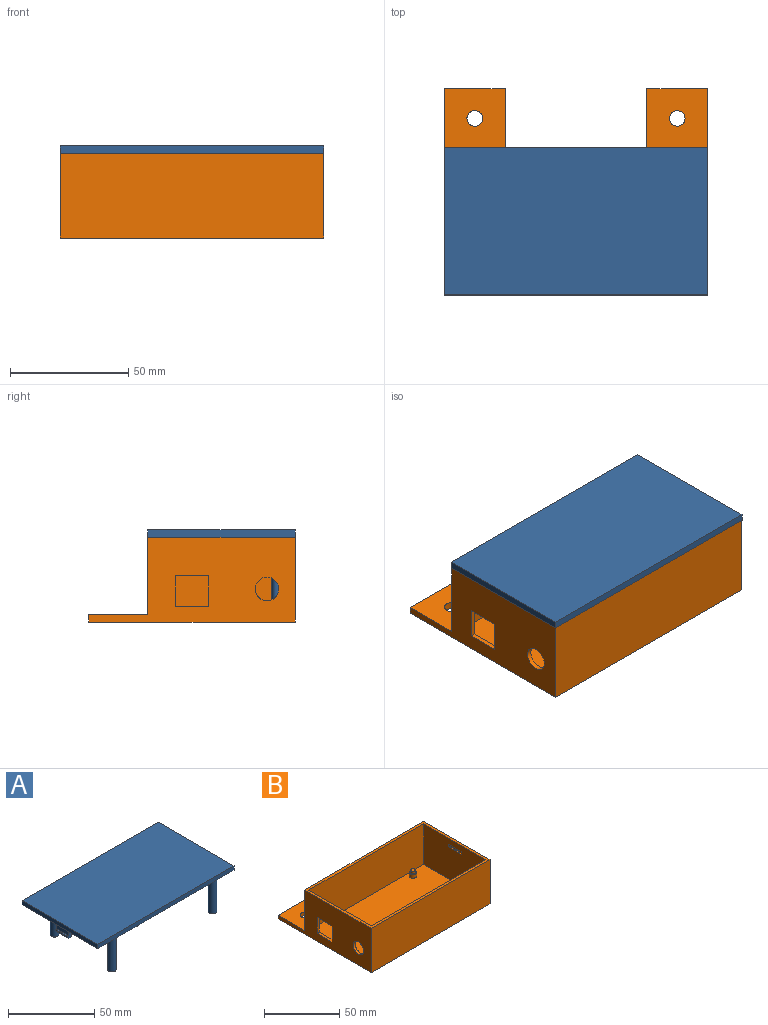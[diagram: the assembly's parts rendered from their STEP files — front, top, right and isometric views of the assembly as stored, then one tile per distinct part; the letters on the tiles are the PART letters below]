
ASSEMBLY  parts=2 mates=1
PART A: 50 faces, bbox 111.6x62.3x31 mm
  f0: plane 111.6x62.34mm, normal (0,0,-1), area 6748.6mm2, adj f1,f2,f3,f4,f10,f11,f12,f13
  f1: plane 111.6x3mm, normal (0,1,0), area 334.8mm2, adj f0,f2,f4,f5
  f2: plane 62.34x3mm, normal (-1,0,0), area 187mm2, adj f0,f1,f3,f5
  f3: plane 111.6x3mm, normal (0,-1,0), area 334.8mm2, adj f0,f2,f4,f5
  f4: plane 62.34x3mm, normal (1,0,0), area 187mm2, adj f0,f1,f3,f5
  f5: plane 111.6x62.34mm, normal (0,0,1), area 6957.1mm2, adj f1,f2,f3,f4
  f6: plane 10x2.5mm, normal (0,0,-1), area 25mm2, adj f7,f11,f12,f13
  f7: plane 10x1mm, normal (0.71,0,-0.71), area 14.1mm2, adj f6,f8,f12,f13
  f8: plane 10x1mm, normal (1,0,0), area 10mm2, adj f7,f9,f12,f13
  f9: plane 10x1mm, normal (0,0,1), area 10mm2, adj f8,f10,f12,f13
  f10: plane 10x5mm, normal (1,0,0), area 50mm2, adj f0,f9,f12,f13
  f11: plane 10x7mm, normal (-1,0,0), area 70mm2, adj f0,f6,f12,f13
  f12: plane 7x3.5mm, normal (0,-1,0), area 19mm2, adj f0,f6,f7,f8,f9,f10,f11
  f13: plane 7x3.5mm, normal (0,1,0), area 19mm2, adj f0,f6,f7,f8,f9,f10,f11
  f14: plane 10x5mm, normal (-1,0,0), area 50mm2, adj f0,f15,f20,f21
  f15: plane 10x1mm, normal (0,0,1), area 10mm2, adj f14,f16,f20,f21
  f16: plane 10x1mm, normal (-1,0,0), area 10mm2, adj f15,f17,f20,f21
  f17: plane 10x1mm, normal (-0.71,0,-0.71), area 14.1mm2, adj f16,f18,f20,f21
  f18: plane 10x2.5mm, normal (0,0,-1), area 25mm2, adj f17,f19,f20,f21
  f19: plane 10x7mm, normal (1,0,0), area 70mm2, adj f0,f18,f20,f21
  f20: plane 7x3.5mm, normal (0,-1,0), area 19mm2, adj f0,f14,f15,f16,f17,f18,f19
  f21: plane 7x3.5mm, normal (0,1,0), area 19mm2, adj f0,f14,f15,f16,f17,f18,f19
  f22: plane 2x2mm, normal (-1,0,0), area 4mm2, adj f0,f23,f25,f26
  f23: plane 10x2mm, normal (0,-1,0), area 20mm2, adj f0,f22,f24,f26
  f24: plane 2x2mm, normal (1,0,0), area 4mm2, adj f0,f23,f25,f26
  f25: plane 10x2mm, normal (0,1,0), area 20mm2, adj f0,f22,f24,f26
  f26: plane 10x2mm, normal (0,0,-1), area 20mm2, adj f22,f23,f24,f25
  f27: plane 2x2mm, normal (-1,0,0), area 4mm2, adj f0,f28,f30,f31
  f28: plane 10x2mm, normal (0,-1,0), area 20mm2, adj f0,f27,f29,f31
  f29: plane 2x2mm, normal (1,0,0), area 4mm2, adj f0,f28,f30,f31
  f30: plane 10x2mm, normal (0,1,0), area 20mm2, adj f0,f27,f29,f31
  f31: plane 10x2mm, normal (0,0,-1), area 20mm2, adj f27,f28,f29,f30
  f32: plane 2x2mm, normal (1,0,0), area 4mm2, adj f0,f33,f35,f36
  f33: plane 10x2mm, normal (0,1,0), area 20mm2, adj f0,f32,f34,f36
  f34: plane 2x2mm, normal (-1,0,0), area 4mm2, adj f0,f33,f35,f36
  f35: plane 10x2mm, normal (0,-1,0), area 20mm2, adj f0,f32,f34,f36
  f36: plane 10x2mm, normal (0,0,-1), area 20mm2, adj f32,f33,f34,f35
  f37: plane 2x2mm, normal (-1,0,0), area 4mm2, adj f0,f38,f40,f41
  f38: plane 10x2mm, normal (0,-1,0), area 20mm2, adj f0,f37,f39,f41
  f39: plane 2x2mm, normal (1,0,0), area 4mm2, adj f0,f38,f40,f41
  f40: plane 10x2mm, normal (0,1,0), area 20mm2, adj f0,f37,f39,f41
  f41: plane 10x2mm, normal (0,0,-1), area 20mm2, adj f37,f38,f39,f40
  f42: plane 5x5mm, normal (0,0,-1), area 19.6mm2, adj f43
  f43: cylinder r=2.5mm len=28mm, axis (0,0,1), area 439.8mm2, adj f0,f42
  f44: plane 5x5mm, normal (0,0,-1), area 19.6mm2, adj f45
  f45: cylinder r=2.5mm len=28mm, axis (0,0,1), area 439.8mm2, adj f0,f44
  f46: plane 5x5mm, normal (0,0,-1), area 19.6mm2, adj f47
  f47: cylinder r=2.5mm len=28mm, axis (0,0,1), area 439.8mm2, adj f0,f46
  f48: plane 5x5mm, normal (0,0,-1), area 19.6mm2, adj f49
  f49: cylinder r=2.5mm len=28mm, axis (0,0,1), area 439.8mm2, adj f0,f48
PART B: 50 faces, bbox 111.6x87.3x36 mm
  f0: plane 58.34x33mm, normal (1,0,0), area 1639.5mm2, adj f2,f11,f13,f14,f25,f26,f27,f28
  f1: plane 87.34x36mm, normal (-1,0,0), area 2058.7mm2, adj f14,f15,f17,f19,f23,f24,f25,f26
  f2: plane 107.6x58.34mm, normal (0,0,1), area 6198.8mm2, adj f0,f3,f5,f7,f9,f11,f12,f13
  f3: cylinder r=2.5mm len=5mm, axis (0,0,-1), area 47.1mm2, adj f2,f4
  f4: plane 5x5mm, normal (0,0,1), area 12.6mm2, adj f3,f40
  f5: cylinder r=2.5mm len=5mm, axis (0,0,-1), area 47.1mm2, adj f2,f6
  f6: plane 5x5mm, normal (0,0,1), area 12.6mm2, adj f5,f42
  f7: cylinder r=2.5mm len=5mm, axis (0,0,-1), area 47.1mm2, adj f2,f8
  f8: plane 5x5mm, normal (0,0,1), area 12.6mm2, adj f7,f44
  f9: cylinder r=2.5mm len=5mm, axis (0,0,-1), area 47.1mm2, adj f2,f10
  f10: plane 5x5mm, normal (0,0,1), area 12.6mm2, adj f9,f46
  f11: plane 107.6x33mm, normal (0,-1,0), area 3550.8mm2, adj f0,f2,f12,f14
  f12: plane 58.34x33mm, normal (-1,0,0), area 1900mm2, adj f2,f11,f13,f14,f30,f32,f33,f34
  f13: plane 107.6x33mm, normal (0,1,0), area 3550.8mm2, adj f0,f2,f12,f14
  f14: plane 111.6x62.34mm, normal (0,0,1), area 679.8mm2, adj f0,f1,f11,f12,f13,f19,f22,f23
  f15: plane 25.8x3mm, normal (0,1,0), area 77.4mm2, adj f1,f16,f17,f24
  f16: plane 25x3mm, normal (1,0,0), area 75mm2, adj f15,f17,f19,f24
  f17: plane 111.6x87.34mm, normal (0,0,-1), area 8178.7mm2, adj f1,f15,f16,f18,f19,f20,f22,f23
  f18: plane 25.8x3mm, normal (0,1,0), area 77.4mm2, adj f17,f20,f21,f22
  f19: plane 111.6x36mm, normal (0,1,0), area 3862.8mm2, adj f1,f14,f16,f17,f20,f21,f22,f24
  f20: plane 25x3mm, normal (-1,0,0), area 75mm2, adj f17,f18,f19,f21
  f21: plane 25.8x25mm, normal (0,0,1), area 610.8mm2, adj f18,f19,f20,f22,f49
  f22: plane 87.34x36mm, normal (1,0,0), area 2319.2mm2, adj f14,f17,f18,f19,f21,f23
  f23: plane 111.6x36mm, normal (0,-1,0), area 4017.6mm2, adj f1,f14,f17,f22
  f24: plane 25.8x25mm, normal (0,0,1), area 610.8mm2, adj f1,f15,f16,f19,f48
  f25: cylinder r=5mm len=10mm, axis (-1,0,0), area 62.8mm2, adj f0,f1
  f26: plane 13x2mm, normal (0,-1,0), area 26mm2, adj f0,f1,f27,f29
  f27: plane 14x2mm, normal (0,0,1), area 28mm2, adj f0,f1,f26,f28
  f28: plane 13x2mm, normal (0,1,0), area 26mm2, adj f0,f1,f27,f29
  f29: plane 14x2mm, normal (0,0,-1), area 28mm2, adj f0,f1,f26,f28
  f30: plane 12x1mm, normal (0,0,1), area 12mm2, adj f12,f31,f33,f34
  f31: plane 12x2.1mm, normal (-1,0,0), area 25.2mm2, adj f30,f32,f33,f34
  f32: plane 12x1mm, normal (0,0,-1), area 12mm2, adj f12,f31,f33,f34
  f33: plane 2.1x1mm, normal (0,-1,0), area 2.1mm2, adj f12,f30,f31,f32
  f34: plane 2.1x1mm, normal (0,1,0), area 2.1mm2, adj f12,f30,f31,f32
  f35: plane 12x1mm, normal (0,0,-1), area 12mm2, adj f0,f36,f38,f39
  f36: plane 12x2.1mm, normal (1,0,0), area 25.2mm2, adj f35,f37,f38,f39
  f37: plane 12x1mm, normal (0,0,1), area 12mm2, adj f0,f36,f38,f39
  f38: plane 2.1x1mm, normal (0,-1,0), area 2.1mm2, adj f0,f35,f36,f37
  f39: plane 2.1x1mm, normal (0,1,0), area 2.1mm2, adj f0,f35,f36,f37
  f40: cylinder r=1.5mm len=3mm, axis (0,0,-1), area 18.8mm2, adj f4,f41
  f41: plane 3x3mm, normal (0,0,1), area 7.1mm2, adj f40
  f42: cylinder r=1.5mm len=3mm, axis (0,0,-1), area 18.8mm2, adj f6,f43
  f43: plane 3x3mm, normal (0,0,1), area 7.1mm2, adj f42
  f44: cylinder r=1.5mm len=3mm, axis (0,0,-1), area 18.8mm2, adj f8,f45
  f45: plane 3x3mm, normal (0,0,1), area 7.1mm2, adj f44
  f46: cylinder r=1.5mm len=3mm, axis (0,0,-1), area 18.8mm2, adj f10,f47
  f47: plane 3x3mm, normal (0,0,1), area 7.1mm2, adj f46
  f48: cylinder r=3.3mm len=6.6mm, axis (0,0,1), area 62.2mm2, adj f17,f24
  f49: cylinder r=3.3mm len=6.6mm, axis (0,0,1), area 62.2mm2, adj f17,f21
PLACE A t=(-170.57,93.9,115.23)mm
PLACE B t=(-137.67,104.06,82.23)mm
MATE fastened A.f0 <-> B.f14  axis (0,0,-1) through (-205.32,130.76,115.23)mm
